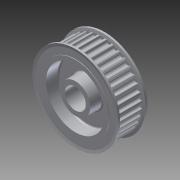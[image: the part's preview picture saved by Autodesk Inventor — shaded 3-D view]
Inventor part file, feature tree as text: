
AUTODESK INVENTOR PART (.ipt)
format: ipt  version: 2014 (Build 180170000, 170)  size: 1,108,992 bytes
history: native  units: in
note: dims shown in document units (in); Inventor stores cm internally (conversion verified against a paired STEP export)
features: mirror x1, other x1, extrude x1, imported_body x1, sketch x1
ambient origin geometry x8: Origin, YZ Plane, XZ Plane, XY Plane, X Axis, Y Axis, Z Axis, Center Point
bodies: Body1 (feature_tree)
feature tree (5):
  mirror  "Mirror1"
  other  "217-3232-STEP1"
  extrude  "Extrusion1"  [1 undecoded]
  imported_body  "Base1"
  sketch  "Sketch1"  dims[d0=39.3701in d1=0.0in]
note: 1 required parameter value undecoded (feature->parameter linkage not recoverable at this tier; creation-order binding heuristic only, values carry confidence <= 0.55)
